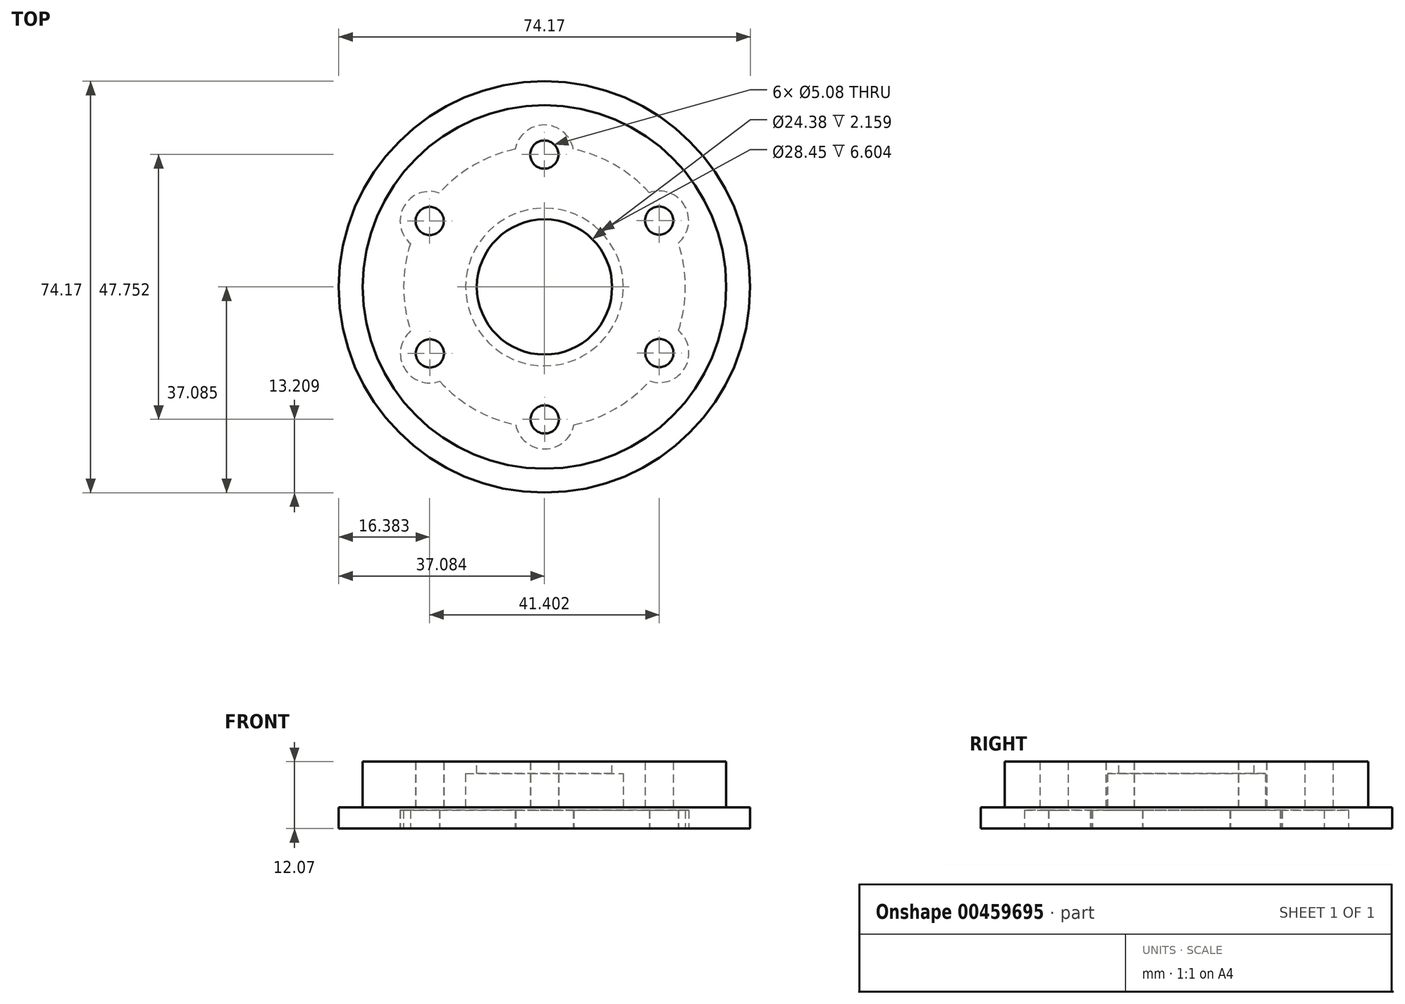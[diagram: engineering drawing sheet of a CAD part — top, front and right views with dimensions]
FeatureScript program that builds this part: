
annotation { "Feature Type Name" : "Feature", "Feature Type Description" : "" }
export const myFeature = defineFeature(function(context is Context, id is Id, definition is map)
    precondition{}
    {
        {
            var Q0;
            Q0=qCreatedBy(makeId("Top.planeOp"),FACE);
            var sketch = newSketch(context, id + "F0", { "sketchPlane" : qUnion([Q0])});
            skCircle(sketch, "E0", {"center": v(44.63, -8.31) * mm, "radius": 37.08 * mm});
            skSolve(sketch);
        }
        {
            var Q0;
            Q0=makeQuery(id+"F0.imprint","IMPRINT",FACE,{"disambiguationData":[TD([[makeQuery(id+"F0.imprint","IMPRINT",EDGE,{"derivedFrom":sQuery(id+"F0.wireOp",EDGE,"E0")}),1.0]])]});
            extrude(context, id + "F1", {"entities" : qUnion([Q0]), "depth" : 3.8 * mm});
        }
        {
            var Q0;
            Q0=makeQuery(id+"F1.opExtrude","CAP_FACE",FACE,{"disambiguationData":[OSD([sQuery(id+"F0.wireOp",EDGE,"E0")])],"isStart":false});
            var sketch = newSketch(context, id + "F2", { "sketchPlane" : qUnion([Q0])});
            skCircle(sketch, "E1", {"center": v(44.63, -8.31) * mm, "radius": 32.77 * mm});
            skSolve(sketch);
        }
        {
            var Q0;
            Q0=makeQuery(id+"F2.imprint","IMPRINT",FACE,{"disambiguationData":[TD([[makeQuery(id+"F2.imprint","IMPRINT",EDGE,{"derivedFrom":sQuery(id+"F2.wireOp",EDGE,"E1")}),1.0]])]});
            extrude(context, id + "F3", {"entities" : qUnion([Q0]), "operationType" : NewBodyOperationType.ADD, "depth" : 8.25 * mm});
        }
        {
            var Q0;
            Q0=makeQuery(id+"F3.opExtrude","CAP_FACE",FACE,{"disambiguationData":[OSD([sQuery(id+"F2.wireOp",EDGE,"E1")])],"isStart":false});
            var sketch = newSketch(context, id + "F4", { "sketchPlane" : qUnion([Q0])});
            skCircle(sketch, "E2", {"center": v(44.63, -8.31) * mm, "radius": 12.2 * mm});
            skSolve(sketch);
        }
        {
            var Q0;
            Q0=makeQuery(id+"F4.imprint","IMPRINT",FACE,{"disambiguationData":[TD([[makeQuery(id+"F4.imprint","IMPRINT",EDGE,{"derivedFrom":sQuery(id+"F4.wireOp",EDGE,"E2")}),1.0]])]});
            extrude(context, id + "F5", {"entities" : qUnion([Q0]), "operationType" : NewBodyOperationType.REMOVE, "oppositeDirection" : true, "depth" : 12.06 * mm});
        }
        {
            var Q0;
            Q0=makeQuery(id+"F1.opExtrude","CAP_FACE",FACE,{"disambiguationData":[OSD([sQuery(id+"F0.wireOp",EDGE,"E0")])],"isStart":true});
            var sketch = newSketch(context, id + "F6", { "sketchPlane" : qUnion([Q0])});
            skCircle(sketch, "E3", {"center": v(44.63, 8.31) * mm, "radius": 25.4 * mm});
            skSolve(sketch);
        }
        {
            var Q0;
            Q0=makeQuery(id+"F6.imprint","IMPRINT",FACE,{"disambiguationData":[TD([[makeQuery(id+"F6.imprint","IMPRINT",EDGE,{"derivedFrom":sQuery(id+"F6.wireOp",EDGE,"E3")}),1.0]])]});
            extrude(context, id + "F7", {"entities" : qUnion([Q0]), "operationType" : NewBodyOperationType.REMOVE, "oppositeDirection" : true, "depth" : 3.3 * mm});
        }
        {
            var Q0;
            Q0=makeQuery(id+"F7.boolean.opBoolean","COPY",FACE,{"derivedFrom":makeQuery(id+"F7.opExtrude","CAP_FACE",FACE,{"disambiguationData":[OSD([sQuery(id+"F6.wireOp",EDGE,"E3")])],"isStart":false})});
            var sketch = newSketch(context, id + "F8", { "sketchPlane" : qUnion([Q0])});
            skCircle(sketch, "E4", {"center": v(44.63, 8.31) * mm, "radius": 14.22 * mm});
            skSolve(sketch);
        }
        {
            var Q0;
            Q0=makeQuery(id+"F8.imprint","IMPRINT",FACE,{"disambiguationData":[TD([[makeQuery(id+"F8.imprint","IMPRINT",EDGE,{"derivedFrom":sQuery(id+"F8.wireOp",EDGE,"E4")}),1.0]])]});
            extrude(context, id + "F9", {"entities" : qUnion([Q0]), "operationType" : NewBodyOperationType.REMOVE, "oppositeDirection" : true, "depth" : 6.6 * mm});
        }
        {
            var Q0;
            Q0=makeQuery(id+"F1.opExtrude","CAP_FACE",FACE,{"disambiguationData":[OSD([sQuery(id+"F0.wireOp",EDGE,"E0")])],"isStart":true});
            var sketch = newSketch(context, id + "F10", { "sketchPlane" : qUnion([Q0])});
            skPoint(sketch, "E5.0.midPoint", {"position": v(54.94, -9.61) * mm});
            skCircle(sketch, "E6", {"center": v(65.33, 20.21) * mm, "radius": 2.54 * mm});
            skCircle(sketch, "E7", {"center": v(65.29, -3.66) * mm, "radius": 2.54 * mm});
            skCircle(sketch, "E8", {"center": v(44.59, -15.56) * mm, "radius": 2.54 * mm});
            skCircle(sketch, "E9", {"center": v(23.93, -3.58) * mm, "radius": 2.54 * mm});
            skCircle(sketch, "E10", {"center": v(23.98, 20.3) * mm, "radius": 2.54 * mm});
            skCircle(sketch, "E11", {"center": v(44.68, 32.2) * mm, "radius": 2.54 * mm});
            skCircle(sketch, "E12", {"center": v(44.68, 32.2) * mm, "radius": 5.33 * mm});
            skCircle(sketch, "E13", {"center": v(65.33, 20.21) * mm, "radius": 5.33 * mm});
            skCircle(sketch, "E14", {"center": v(65.29, -3.66) * mm, "radius": 5.33 * mm});
            skCircle(sketch, "E15", {"center": v(44.59, -15.56) * mm, "radius": 5.33 * mm});
            skCircle(sketch, "E16", {"center": v(23.93, -3.58) * mm, "radius": 5.33 * mm});
            skCircle(sketch, "E17", {"center": v(23.98, 20.3) * mm, "radius": 5.33 * mm});
            skSolve(sketch);
        }
        {
            var Q0;
            {var subQ0=sQuery(id+"F10.wireOp",EDGE,"E9");var subQ1=makeQuery(id+"F7.boolean.opBoolean","COPY",EDGE,{"derivedFrom":makeQuery(id+"F7.opExtrude","CAP_EDGE",EDGE,{"disambiguationData":[OSD([sQuery(id+"F6.wireOp",EDGE,"E3")])],"isStart":true})});var subQ2=makeQuery(id+"F10.imprint","INTERSECT",VERTEX,{"disambiguationData":[OD(0.0)],"derivedFrom":[subQ1,subQ0]});Q0=makeQuery(id+"F10.imprint","IMPRINT",FACE,{"disambiguationData":[TD([[makeQuery(id+"F10.imprint","IMPRINT",EDGE,{"disambiguationData":[TD([[subQ2,1.0]])],"derivedFrom":subQ0}),1.0]])]});}
            var Q1;
            {var subQ0=sQuery(id+"F10.wireOp",EDGE,"E9");var subQ1=makeQuery(id+"F7.boolean.opBoolean","COPY",EDGE,{"derivedFrom":makeQuery(id+"F7.opExtrude","CAP_EDGE",EDGE,{"disambiguationData":[OSD([sQuery(id+"F6.wireOp",EDGE,"E3")])],"isStart":true})});var subQ2=makeQuery(id+"F10.imprint","INTERSECT",VERTEX,{"disambiguationData":[OD(0.0)],"derivedFrom":[subQ1,subQ0]});Q1=makeQuery(id+"F10.imprint","IMPRINT",FACE,{"disambiguationData":[TD([[makeQuery(id+"F10.imprint","IMPRINT",EDGE,{"disambiguationData":[TD([[subQ2,-1.0]])],"derivedFrom":subQ0}),1.0]])]});}
            var Q2;
            {var subQ0=sQuery(id+"F10.wireOp",EDGE,"E10");var subQ1=makeQuery(id+"F7.boolean.opBoolean","COPY",EDGE,{"derivedFrom":makeQuery(id+"F7.opExtrude","CAP_EDGE",EDGE,{"disambiguationData":[OSD([sQuery(id+"F6.wireOp",EDGE,"E3")])],"isStart":true})});var subQ2=makeQuery(id+"F10.imprint","INTERSECT",VERTEX,{"disambiguationData":[OD(0.0)],"derivedFrom":[subQ1,subQ0]});Q2=makeQuery(id+"F10.imprint","IMPRINT",FACE,{"disambiguationData":[TD([[makeQuery(id+"F10.imprint","IMPRINT",EDGE,{"disambiguationData":[TD([[subQ2,1.0]])],"derivedFrom":subQ0}),1.0]])]});}
            var Q3;
            {var subQ0=sQuery(id+"F10.wireOp",EDGE,"E10");var subQ1=makeQuery(id+"F7.boolean.opBoolean","COPY",EDGE,{"derivedFrom":makeQuery(id+"F7.opExtrude","CAP_EDGE",EDGE,{"disambiguationData":[OSD([sQuery(id+"F6.wireOp",EDGE,"E3")])],"isStart":true})});var subQ2=makeQuery(id+"F10.imprint","INTERSECT",VERTEX,{"disambiguationData":[OD(0.0)],"derivedFrom":[subQ1,subQ0]});Q3=makeQuery(id+"F10.imprint","IMPRINT",FACE,{"disambiguationData":[TD([[makeQuery(id+"F10.imprint","IMPRINT",EDGE,{"disambiguationData":[TD([[subQ2,-1.0]])],"derivedFrom":subQ0}),1.0]])]});}
            var Q4;
            {var subQ0=sQuery(id+"F10.wireOp",EDGE,"E11");var subQ1=makeQuery(id+"F7.boolean.opBoolean","COPY",EDGE,{"derivedFrom":makeQuery(id+"F7.opExtrude","CAP_EDGE",EDGE,{"disambiguationData":[OSD([sQuery(id+"F6.wireOp",EDGE,"E3")])],"isStart":true})});var subQ2=makeQuery(id+"F10.imprint","INTERSECT",VERTEX,{"disambiguationData":[OD(0.0)],"derivedFrom":[subQ1,subQ0]});Q4=makeQuery(id+"F10.imprint","IMPRINT",FACE,{"disambiguationData":[TD([[makeQuery(id+"F10.imprint","IMPRINT",EDGE,{"disambiguationData":[TD([[subQ2,1.0]])],"derivedFrom":subQ0}),1.0]])]});}
            var Q5;
            {var subQ0=sQuery(id+"F10.wireOp",EDGE,"E11");var subQ1=makeQuery(id+"F7.boolean.opBoolean","COPY",EDGE,{"derivedFrom":makeQuery(id+"F7.opExtrude","CAP_EDGE",EDGE,{"disambiguationData":[OSD([sQuery(id+"F6.wireOp",EDGE,"E3")])],"isStart":true})});var subQ2=makeQuery(id+"F10.imprint","INTERSECT",VERTEX,{"disambiguationData":[OD(0.0)],"derivedFrom":[subQ1,subQ0]});Q5=makeQuery(id+"F10.imprint","IMPRINT",FACE,{"disambiguationData":[TD([[makeQuery(id+"F10.imprint","IMPRINT",EDGE,{"disambiguationData":[TD([[subQ2,-1.0]])],"derivedFrom":subQ0}),1.0]])]});}
            var Q6;
            {var subQ0=sQuery(id+"F10.wireOp",EDGE,"E6");var subQ1=makeQuery(id+"F7.boolean.opBoolean","COPY",EDGE,{"derivedFrom":makeQuery(id+"F7.opExtrude","CAP_EDGE",EDGE,{"disambiguationData":[OSD([sQuery(id+"F6.wireOp",EDGE,"E3")])],"isStart":true})});var subQ2=makeQuery(id+"F10.imprint","INTERSECT",VERTEX,{"disambiguationData":[OD(0.0)],"derivedFrom":[subQ1,subQ0]});Q6=makeQuery(id+"F10.imprint","IMPRINT",FACE,{"disambiguationData":[TD([[makeQuery(id+"F10.imprint","IMPRINT",EDGE,{"disambiguationData":[TD([[subQ2,1.0]])],"derivedFrom":subQ0}),1.0]])]});}
            var Q7;
            {var subQ0=sQuery(id+"F10.wireOp",EDGE,"E6");var subQ1=makeQuery(id+"F7.boolean.opBoolean","COPY",EDGE,{"derivedFrom":makeQuery(id+"F7.opExtrude","CAP_EDGE",EDGE,{"disambiguationData":[OSD([sQuery(id+"F6.wireOp",EDGE,"E3")])],"isStart":true})});var subQ2=makeQuery(id+"F10.imprint","INTERSECT",VERTEX,{"disambiguationData":[OD(0.0)],"derivedFrom":[subQ1,subQ0]});Q7=makeQuery(id+"F10.imprint","IMPRINT",FACE,{"disambiguationData":[TD([[makeQuery(id+"F10.imprint","IMPRINT",EDGE,{"disambiguationData":[TD([[subQ2,-1.0]])],"derivedFrom":subQ0}),1.0]])]});}
            var Q8;
            {var subQ0=sQuery(id+"F10.wireOp",EDGE,"E7");var subQ1=makeQuery(id+"F7.boolean.opBoolean","COPY",EDGE,{"derivedFrom":makeQuery(id+"F7.opExtrude","CAP_EDGE",EDGE,{"disambiguationData":[OSD([sQuery(id+"F6.wireOp",EDGE,"E3")])],"isStart":true})});var subQ2=makeQuery(id+"F10.imprint","INTERSECT",VERTEX,{"disambiguationData":[OD(0.0)],"derivedFrom":[subQ1,subQ0]});Q8=makeQuery(id+"F10.imprint","IMPRINT",FACE,{"disambiguationData":[TD([[makeQuery(id+"F10.imprint","IMPRINT",EDGE,{"disambiguationData":[TD([[subQ2,-1.0]])],"derivedFrom":subQ0}),1.0]])]});}
            var Q9;
            {var subQ0=sQuery(id+"F10.wireOp",EDGE,"E7");var subQ1=makeQuery(id+"F7.boolean.opBoolean","COPY",EDGE,{"derivedFrom":makeQuery(id+"F7.opExtrude","CAP_EDGE",EDGE,{"disambiguationData":[OSD([sQuery(id+"F6.wireOp",EDGE,"E3")])],"isStart":true})});var subQ2=makeQuery(id+"F10.imprint","INTERSECT",VERTEX,{"disambiguationData":[OD(0.0)],"derivedFrom":[subQ1,subQ0]});Q9=makeQuery(id+"F10.imprint","IMPRINT",FACE,{"disambiguationData":[TD([[makeQuery(id+"F10.imprint","IMPRINT",EDGE,{"disambiguationData":[TD([[subQ2,1.0]])],"derivedFrom":subQ0}),1.0]])]});}
            var Q10;
            {var subQ0=sQuery(id+"F10.wireOp",EDGE,"E8");var subQ1=makeQuery(id+"F7.boolean.opBoolean","COPY",EDGE,{"derivedFrom":makeQuery(id+"F7.opExtrude","CAP_EDGE",EDGE,{"disambiguationData":[OSD([sQuery(id+"F6.wireOp",EDGE,"E3")])],"isStart":true})});var subQ2=makeQuery(id+"F10.imprint","INTERSECT",VERTEX,{"disambiguationData":[OD(0.0)],"derivedFrom":[subQ1,subQ0]});Q10=makeQuery(id+"F10.imprint","IMPRINT",FACE,{"disambiguationData":[TD([[makeQuery(id+"F10.imprint","IMPRINT",EDGE,{"disambiguationData":[TD([[subQ2,-1.0]])],"derivedFrom":subQ0}),1.0]])]});}
            var Q11;
            {var subQ0=sQuery(id+"F10.wireOp",EDGE,"E8");var subQ1=makeQuery(id+"F7.boolean.opBoolean","COPY",EDGE,{"derivedFrom":makeQuery(id+"F7.opExtrude","CAP_EDGE",EDGE,{"disambiguationData":[OSD([sQuery(id+"F6.wireOp",EDGE,"E3")])],"isStart":true})});var subQ2=makeQuery(id+"F10.imprint","INTERSECT",VERTEX,{"disambiguationData":[OD(0.0)],"derivedFrom":[subQ1,subQ0]});Q11=makeQuery(id+"F10.imprint","IMPRINT",FACE,{"disambiguationData":[TD([[makeQuery(id+"F10.imprint","IMPRINT",EDGE,{"disambiguationData":[TD([[subQ2,1.0]])],"derivedFrom":subQ0}),1.0]])]});}
            extrude(context, id + "F11", {"entities" : qUnion([Q0, Q1, Q2, Q3, Q4, Q5, Q6, Q7, Q8, Q9, Q10, Q11]), "operationType" : NewBodyOperationType.REMOVE, "oppositeDirection" : true, "depth" : 12.2 * mm});
        }
        {
            var Q0;
            Q0 = qSketchRegion(id + "F10", true);
            extrude(context, id + "F12", {"entities" : qUnion([Q0]), "operationType" : NewBodyOperationType.REMOVE, "oppositeDirection" : true, "depth" : 3.3 * mm});
        }
    });
